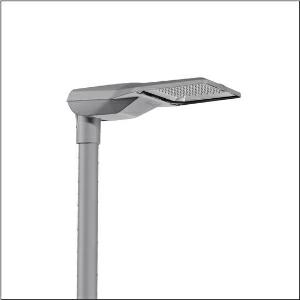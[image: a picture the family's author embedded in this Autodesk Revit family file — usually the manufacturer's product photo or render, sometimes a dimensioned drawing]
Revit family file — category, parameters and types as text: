
# Revit family: streetlight_sl_21_iq_midi___stw1_0a_5xe3e61d08nb_dcea
name_source: partatom
category: Lighting Fixtures
units: mm (PartAtom-declared; Revit-internal decimal feet)

## family parameters
Cut with Voids When Loaded = No
Host = Face
Light Source = No
Part Type = Normal
Room Calculation Point = No
Round Connector Dimension = Use Diameter
Shared = No

## types (1)
- --- (1 x LED, 20820 lm, 155.5 W, 2700K)
    Apparent Load = 155 VA
    CIE Flux Codes = 39 75 98 100 100
    Color Rendering = 70
    Color Temperature = 2700K
    Default Elevation = 1800 mm
    Description = Streetlight SL 21 iQ midi, mast luminaire, primary light control with lens, of PMMA, primary optical cover: cover, of toughened safety glass, transparent, light distribution: STW1.0a, light emission: direct distribution, primary light characteristic: asymmetric, installation type: post-top, side-entry, LED, High Power LED, rated luminous flux: 20.820lm, luminous efficacy: 134lm/W, light colour: 727, colour temperature: 2700K, control: Auto-Match, Temp-Guard, Lumen-Switch, Night-Set, Smart-Wire, Light-Fading, Desk-Remote (wireless, voltage-free reading and setting of iQ features in the workshop via application-optimized NFC function/RFID function), optimised constant luminous flux control (CLO 2.0), presetting dimming linear, mains connection: 230..240V, AC, 50/60Hz, start of lifetime: 156W, end of service life: 162W, reduction: 69W, luminaire housing, of diecast aluminium, powder-coated, Siteco® metallic grey (DB 702S), corrosivity category C5 mid according to DIN EN ISO 12944, please order mast flange separately, inclination adjustable: 0°, 5°, 10°, 15°, sealing non-destructively replaceable, multi-level sealing system, length: 644mm, width: 335mm, height: 110mm, mast flange for spigot size: 42mm (side-entry): 5XC10008XM4, 60/48mm (side-entry/post-top): 5XC10108XM2, 76/60mm (side-entry/post-top): 5XC10108XM1, protection rating (complete): IP66, insulation class (complete): insulation class II (safety insulation), certification: CE, ENEC, ENEC+, VDE, impact resistance: IK09, permissible operating ambient temperature for outdoor applications: -40..+50°C, standard-compliant lighting for roads and squares, packaging unit: 1 piece

Light Distribution: STW1.0a
    Height = 111 mm
    Lamp = 1 x LED
    Lamp Light Flux = 20820 lm
    Lamp Power = 155.5 W
    Lamp count = 1
    Length = 644 mm
    Luminous efficacy = 134 lm/W
    Manufacturer = Siteco
    ModVariant = No
    Model = 5XE3E61D08NB
    Number of Poles = 1
    OnlyDefault = Yes
    Power Factor = 1
    Product Name = Streetlight SL 21 iQ midi | STW1.0a
    Product group = mast luminaire | pylon top
    ProductGroupID = 6100
    Protection Class = Protection class II
    Protection Degree = IP 66
    RLX_Detail_Level = 1
    RLX_Emergency_Light_Flux = 0 lm
    RLX_Emergency_Type = 0
    RLX_Emergency_Type_DB = No
    RlxData = <blob elided: 91369 chars, md5=6eabd884>
    Socket = socket
    Standby Power = 0 W
    System Light Flux = 20820 lm
    System Power = 155 W
    Type Comments = factory setting: luminous flux: 100 % | dim-lin: 254 | 823 mA
    Type Image = l_1004298.jpg
    URL = http://relux.com
    VarID = @adj_120197
    Voltage = 0 V
    Weight = 0.00 kg
    Width = 336 mm

## geometry (parser evidence)
native form markers: Blend x4, Sweep x10
no freeform markers — native parametric forms only
